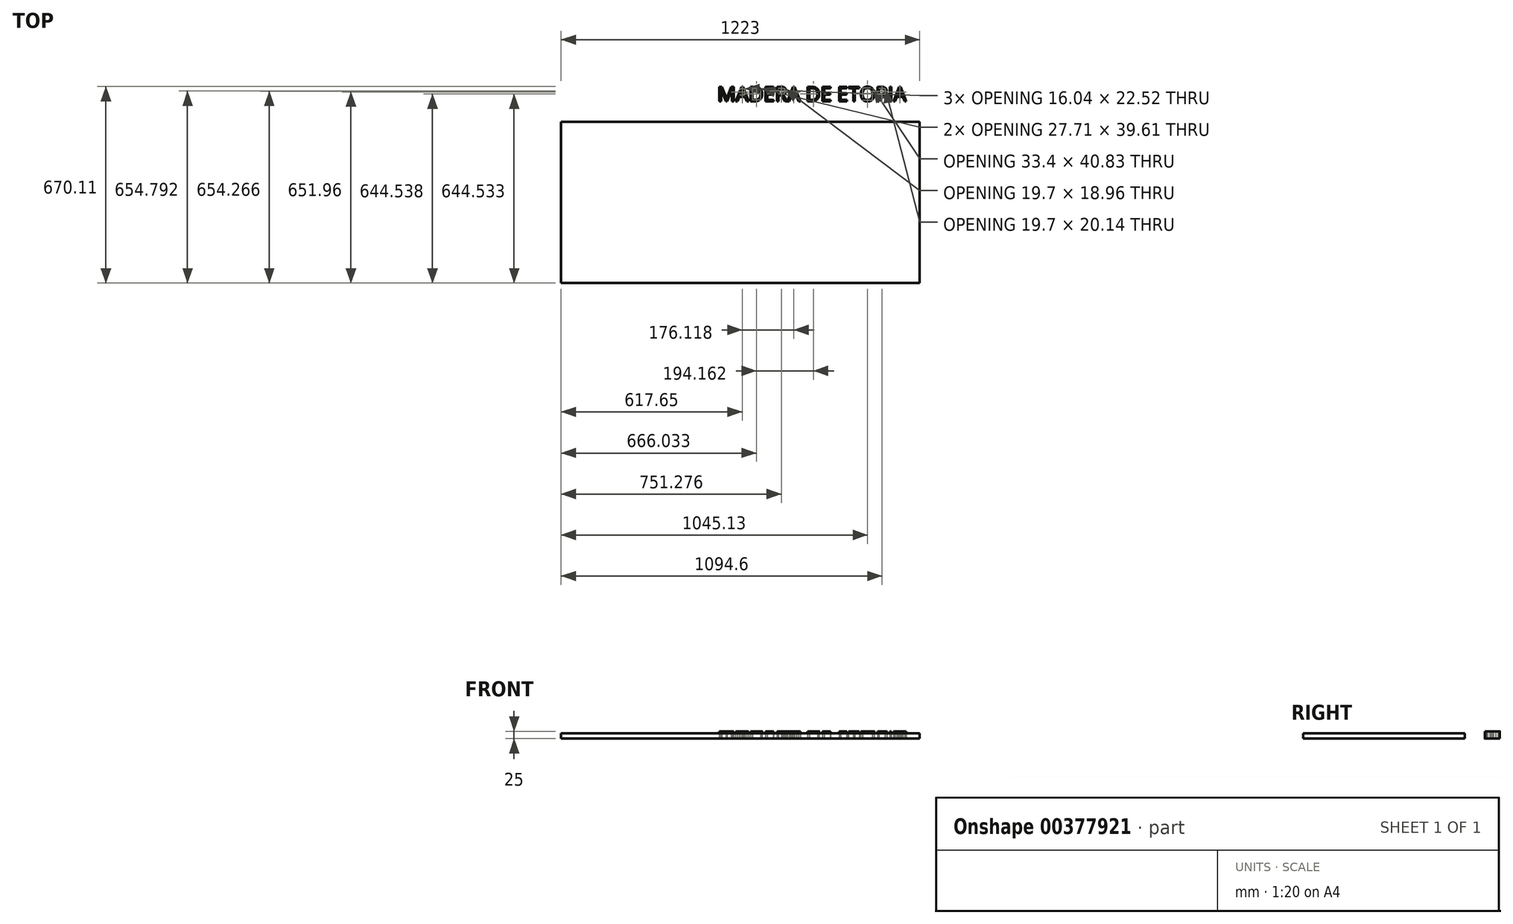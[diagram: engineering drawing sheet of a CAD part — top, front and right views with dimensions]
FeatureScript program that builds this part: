
annotation { "Feature Type Name" : "Feature", "Feature Type Description" : "" }
export const myFeature = defineFeature(function(context is Context, id is Id, definition is map)
    precondition{}
    {
        {
            var Q0;
            Q0=qCreatedBy(makeId("Top.planeOp"),FACE);
            var sketch = newSketch(context, id + "F0", { "sketchPlane" : qUnion([Q0])});
            skLineSegment(sketch, "E0.bottom", {"start": v(0, 0) * mm, "end": v(1223, 0) * mm});
            skLineSegment(sketch, "E0.top", {"start": v(0, 550) * mm, "end": v(1223, 550) * mm});
            skLineSegment(sketch, "E0.left", {"start": v(0, 0) * mm, "end": v(0, 550) * mm});
            skLineSegment(sketch, "E0.right", {"start": v(1223, 0) * mm, "end": v(1223, 550) * mm});
            skSolve(sketch);
        }
        {
            var Q0;
            Q0=makeQuery(id+"F0.imprint","IMPRINT",FACE,{"disambiguationData":[TD([[makeQuery(id+"F0.imprint","IMPRINT",EDGE,{"derivedFrom":sQuery(id+"F0.wireOp",EDGE,"E0.bottom")}),1.0]])]});
            extrude(context, id + "F1", {"entities" : qUnion([Q0]), "depth" : 18 * mm, "offsetDistance" : 25 * mm});
        }
        {
            var Q0;
            Q0=qCreatedBy(makeId("Top.planeOp"),FACE);
            var sketch = newSketch(context, id + "F2", { "sketchPlane" : qUnion([Q0])});
            skText(sketch, "E1", { "text": "MADERA DE ETOPIA", "fontName": "OpenSans-Regular.ttf"});
            const initialGuessF2  = {"E1": [0.53296, 0.61975, 1, 0, 0.05]};
            skSetInitialGuess(sketch, initialGuessF2);
            skSolve(sketch);
        }
        {
            var Q0;
            Q0 = qSketchRegion(id + "F2", true);
            extrude(context, id + "F3", {"entities" : qUnion([Q0]), "depth" : 25 * mm, "offsetDistance" : 25 * mm});
        }
    });
